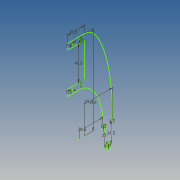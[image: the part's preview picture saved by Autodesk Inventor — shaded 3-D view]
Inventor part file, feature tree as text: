
AUTODESK INVENTOR PART (.ipt)
format: ipt  version: 2014 (Build 180170000, 170)  size: 80,384 bytes
history: native  units: mm
features: sketch x1
ambient origin geometry x8: Origin, YZ Plane, XZ Plane, XY Plane, X Axis, Y Axis, Z Axis, Center Point
feature tree (1):
  sketch  "Sketch1"  dims[d0=33.5mm d1=106.0mm d2=20.5mm d3=28.5mm d4=40.5mm d5=1.5mm d6=1.5mm d7=3.5mm d8=2.0mm d9=2.0mm d10=5.5mm d11=2.0mm d12=5.5mm d13=2.0mm d14=25.0mm d15=24.5mm d16=6.5mm d17=2.0mm]
